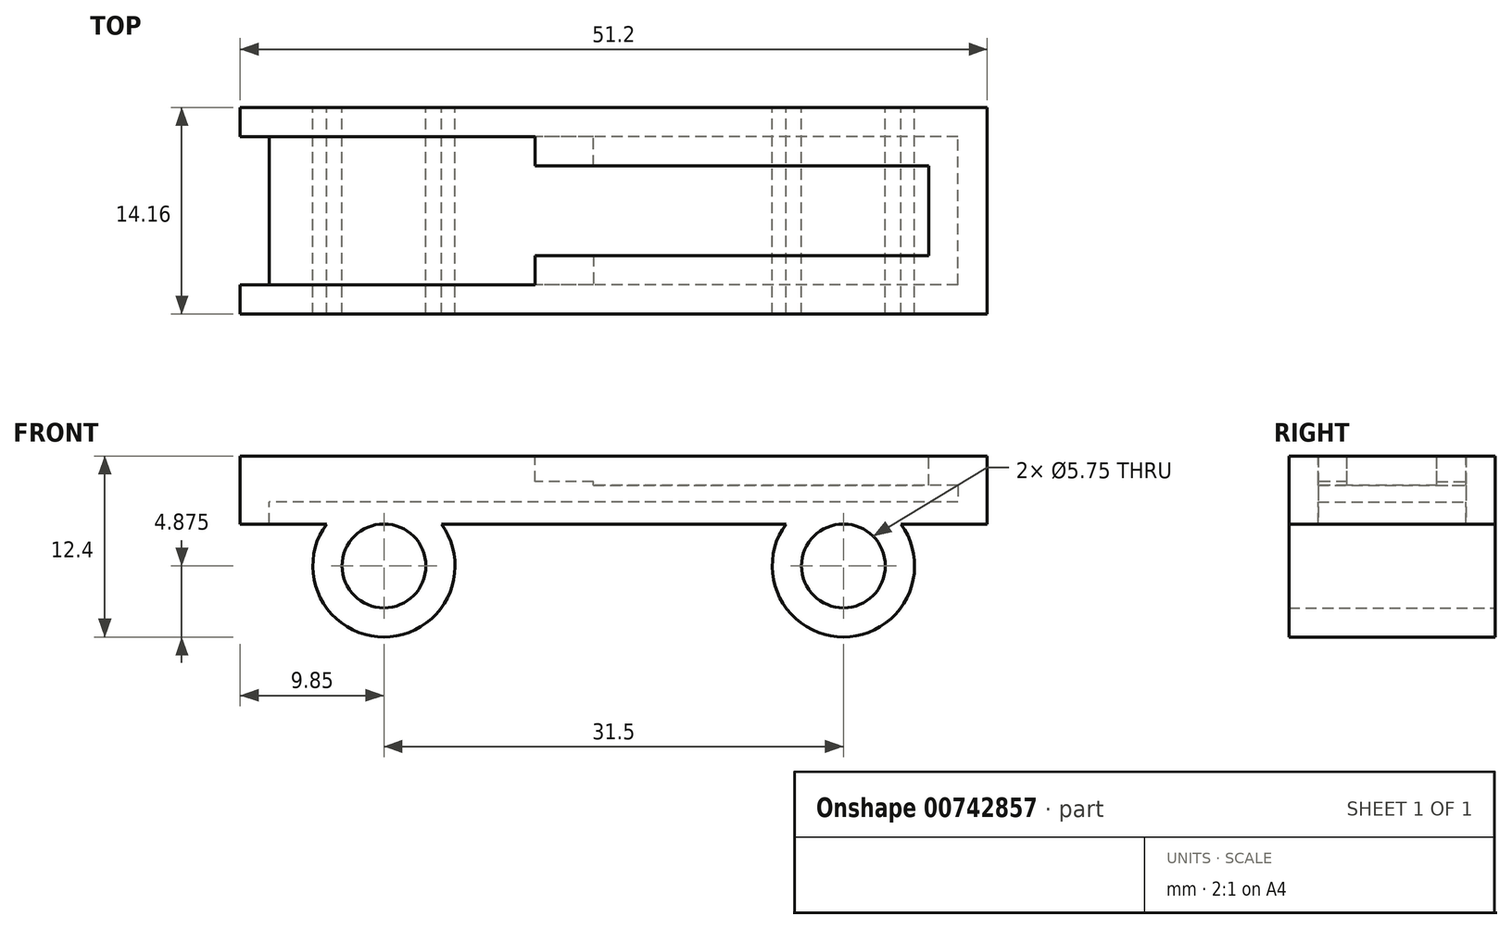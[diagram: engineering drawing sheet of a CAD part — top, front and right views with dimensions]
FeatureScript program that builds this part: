
annotation { "Feature Type Name" : "Feature", "Feature Type Description" : "" }
export const myFeature = defineFeature(function(context is Context, id is Id, definition is map)
    precondition{}
    {
        {
            var Q0;
            Q0=qCreatedBy(makeId("Top.planeOp"),FACE);
            var sketch = newSketch(context, id + "F0", { "sketchPlane" : qUnion([Q0])});
            skLineSegment(sketch, "E0.bottom", {"start": v(23.6, -5.07) * mm, "end": v(-23.6, -5.08) * mm});
            skLineSegment(sketch, "E0.top", {"start": v(23.6, 5.08) * mm, "end": v(-23.6, 5.07) * mm});
            skLineSegment(sketch, "E0.left", {"start": v(23.6, -5.07) * mm, "end": v(23.6, 5.08) * mm});
            skLineSegment(sketch, "E0.right", {"start": v(-23.6, -5.08) * mm, "end": v(-23.6, 5.07) * mm});
            skPoint(sketch, "E0.middle", {"position": v(0, 0) * mm});
            skLineSegment(sketch, "E1.0", {"start": v(-25.6, -7.08) * mm, "end": v(-25.6, 7.07) * mm});
            skLineSegment(sketch, "E1.1", {"start": v(25.6, -7.08) * mm, "end": v(-25.6, -7.08) * mm});
            skLineSegment(sketch, "E1.2", {"start": v(25.6, -7.07) * mm, "end": v(25.6, 7.08) * mm});
            skLineSegment(sketch, "E1.3", {"start": v(25.6, 7.08) * mm, "end": v(-25.6, 7.07) * mm});
            skLineSegment(sketch, "E2", {"start": v(-23.6, 5.07) * mm, "end": v(-25.6, 5.07) * mm});
            skLineSegment(sketch, "E3", {"start": v(-23.6, -5.08) * mm, "end": v(-25.6, -5.08) * mm});
            skSolve(sketch);
        }
        {
            var Q0;
            Q0=makeQuery(id+"F0.imprint","IMPRINT",FACE,{"disambiguationData":[TD([[makeQuery(id+"F0.imprint","IMPRINT",EDGE,{"derivedFrom":sQuery(id+"F0.wireOp",EDGE,"E0.bottom")}),1.0]])]});
            extrude(context, id + "F1", {"entities" : qUnion([Q0]), "depth" : 3.15 * mm, "offsetDistance" : 25 * mm});
        }
        {
            var Q0;
            Q0=makeQuery(id+"F1.opExtrude","CAP_FACE",FACE,{"disambiguationData":[OSD([sQuery(id+"F0.wireOp",EDGE,"E0.bottom"),sQuery(id+"F0.wireOp",EDGE,"E0.top"),sQuery(id+"F0.wireOp",EDGE,"E0.left"),sQuery(id+"F0.wireOp",EDGE,"E1.0"),sQuery(id+"F0.wireOp",EDGE,"E1.1"),sQuery(id+"F0.wireOp",EDGE,"E1.2"),sQuery(id+"F0.wireOp",EDGE,"E1.3"),sQuery(id+"F0.wireOp",EDGE,"E2"),sQuery(id+"F0.wireOp",EDGE,"E3")])],"isStart":false});
            var sketch = newSketch(context, id + "F2", { "sketchPlane" : qUnion([Q0])});
            skLineSegment(sketch, "E4", {"start": v(-25.6, 5.07) * mm, "end": v(-25.6, 3.07) * mm});
            skLineSegment(sketch, "E5", {"start": v(-25.6, 3.07) * mm, "end": v(21.6, 3.07) * mm});
            skLineSegment(sketch, "E6", {"start": v(21.6, 3.07) * mm, "end": v(21.6, -3.07) * mm});
            skLineSegment(sketch, "E7", {"start": v(21.6, -3.07) * mm, "end": v(-25.6, -3.07) * mm});
            skLineSegment(sketch, "E8", {"start": v(-25.6, -3.07) * mm, "end": v(-25.6, -5.08) * mm});
            skLineSegment(sketch, "E9", {"start": v(23.6, -3.07) * mm, "end": v(-1.4, -3.07) * mm});
            skLineSegment(sketch, "E10", {"start": v(-1.4, -3.07) * mm, "end": v(-1.4, -5.08) * mm});
            skLineSegment(sketch, "E11", {"start": v(-1.4, -3.07) * mm, "end": v(-5.4, -3.07) * mm});
            skLineSegment(sketch, "E12", {"start": v(-5.4, -3.07) * mm, "end": v(-5.4, -5.07) * mm});
            skLineSegment(sketch, "E13", {"start": v(-1.4, 3.07) * mm, "end": v(-1.4, 5.07) * mm});
            skLineSegment(sketch, "E14", {"start": v(-5.4, 3.07) * mm, "end": v(-5.4, 5.07) * mm});
            skSolve(sketch);
        }
        {
            var Q0;
            Q0=makeQuery(id+"F0.imprint","IMPRINT",FACE,{"disambiguationData":[TD([[makeQuery(id+"F0.imprint","IMPRINT",EDGE,{"derivedFrom":sQuery(id+"F0.wireOp",EDGE,"E0.bottom")}),-1.0]])]});
            var Q1;
            Q1=makeQuery(id+"F0.imprint","IMPRINT",FACE,{"disambiguationData":[TD([[makeQuery(id+"F0.imprint","IMPRINT",EDGE,{"derivedFrom":sQuery(id+"F0.wireOp",EDGE,"E0.bottom")}),1.0]])]});
            extrude(context, id + "F3", {"entities" : qUnion([Q0, Q1]), "operationType" : NewBodyOperationType.ADD, "oppositeDirection" : true, "depth" : 1.5 * mm, "offsetDistance" : 25 * mm});
        }
        {
            var Q0;
            {var subQ3=sQuery(id+"F2.wireOp",EDGE,"E10");Q0=makeQuery(id+"F2.imprint","IMPRINT",FACE,{"disambiguationData":[TD([[makeQuery(id+"F2.imprint","IMPRINT",EDGE,{"derivedFrom":subQ3}),1.0]])]});}
            var Q1;
            {var subQ2=sQuery(id+"F2.wireOp",EDGE,"E6");Q1=makeQuery(id+"F2.imprint","IMPRINT",FACE,{"disambiguationData":[TD([[makeQuery(id+"F2.imprint","IMPRINT",EDGE,{"derivedFrom":subQ2}),1.0]])]});}
            extrude(context, id + "F4", {"entities" : qUnion([Q0, Q1]), "operationType" : NewBodyOperationType.ADD, "oppositeDirection" : true, "depth" : 2 * mm, "offsetDistance" : 25 * mm});
        }
        {
            var Q0;
            {var subQ0=sQuery(id+"F2.wireOp",EDGE,"E10");Q0=makeQuery(id+"F2.imprint","IMPRINT",FACE,{"disambiguationData":[TD([[makeQuery(id+"F2.imprint","IMPRINT",EDGE,{"derivedFrom":subQ0}),-1.0]])]});}
            var Q1;
            {var subQ0=sQuery(id+"F2.wireOp",EDGE,"E13");Q1=makeQuery(id+"F2.imprint","IMPRINT",FACE,{"disambiguationData":[TD([[makeQuery(id+"F2.imprint","IMPRINT",EDGE,{"derivedFrom":subQ0}),1.0]])]});}
            extrude(context, id + "F5", {"entities" : qUnion([Q0, Q1]), "operationType" : NewBodyOperationType.ADD, "oppositeDirection" : true, "depth" : 1.75 * mm, "offsetDistance" : 25 * mm});
        }
        {
            var Q0;
            {var subQ0=sQuery(id+"F0.wireOp",EDGE,"E1.3");Q0=makeQuery(id+"F3.boolean.opBoolean","MERGE",FACE,{"derivedFrom":[makeQuery(id+"F1.opExtrude","SWEPT_FACE",FACE,{"disambiguationData":[OSD([subQ0])]}),makeQuery(id+"F3.opExtrude","SWEPT_FACE",FACE,{"disambiguationData":[OSD([subQ0])]})]});}
            var sketch = newSketch(context, id + "F6", { "sketchPlane" : qUnion([Q0])});
            skLineSegment(sketch, "E15", {"start": v(-18.25, -1.5) * mm, "end": v(18.25, -1.5) * mm});
            skLineSegment(sketch, "E16", {"start": v(-18.25, -1.5) * mm, "end": v(-15.75, -1.5) * mm});
            skLineSegment(sketch, "E17", {"start": v(18.25, -1.5) * mm, "end": v(15.75, -1.5) * mm});
            skLineSegment(sketch, "E18", {"start": v(15.75, -1.5) * mm, "end": v(15.75, -4.38) * mm});
            skLineSegment(sketch, "E19", {"start": v(-15.75, -1.5) * mm, "end": v(-15.75, -4.38) * mm});
            skLineSegment(sketch, "E20", {"start": v(-12, -1.5) * mm, "end": v(-19.5, -1.5) * mm});
            skLineSegment(sketch, "E21", {"start": v(12, -1.5) * mm, "end": v(19.5, -1.5) * mm});
            skLineSegment(sketch, "E22", {"start": v(17.81, 0) * mm, "end": v(13.69, 0) * mm});
            skLineSegment(sketch, "E23", {"start": v(-13.69, 0) * mm, "end": v(-17.81, 0) * mm});
            skCircle(sketch, "E24", {"center": v(15.75, -4.38) * mm, "radius": 2.88 * mm});
            skCircle(sketch, "E25", {"center": v(-15.75, -4.38) * mm, "radius": 2.88 * mm});
            skCircle(sketch, "E26.0", {"center": v(15.75, -4.38) * mm, "radius": 4.87 * mm});
            skCircle(sketch, "E27.0", {"center": v(-15.75, -4.38) * mm, "radius": 4.88 * mm});
            skLineSegment(sketch, "E28", {"start": v(17.9, 0) * mm, "end": v(17.81, 0) * mm});
            skLineSegment(sketch, "E29", {"start": v(13.69, 0) * mm, "end": v(13.6, 0) * mm});
            skLineSegment(sketch, "E30", {"start": v(-13.6, 0) * mm, "end": v(-13.69, 0) * mm});
            skLineSegment(sketch, "E31", {"start": v(-17.81, 0) * mm, "end": v(-17.9, 0) * mm});
            skSolve(sketch);
        }
        {
            var Q0;
            {var subQ6=sQuery(id+"F6.wireOp",EDGE,"E24");Q0=makeQuery(id+"F6.imprint","IMPRINT",FACE,{"disambiguationData":[TD([[makeQuery(id+"F6.imprint","IMPRINT",EDGE,{"derivedFrom":subQ6}),-1.0]])]});}
            var Q1;
            Q1=makeQuery(id+"F6.imprint","IMPRINT",FACE,{"disambiguationData":[TD([[makeQuery(id+"F6.imprint","IMPRINT",EDGE,{"derivedFrom":sQuery(id+"F6.wireOp",EDGE,"E22")}),1.0]])]});
            var Q2;
            Q2=makeQuery(id+"F6.imprint","IMPRINT",FACE,{"disambiguationData":[TD([[makeQuery(id+"F6.imprint","IMPRINT",EDGE,{"derivedFrom":sQuery(id+"F6.wireOp",EDGE,"E23")}),1.0]])]});
            var Q3;
            {var subQ0=sQuery(id+"F6.wireOp",EDGE,"E25");Q3=makeQuery(id+"F6.imprint","IMPRINT",FACE,{"disambiguationData":[TD([[makeQuery(id+"F6.imprint","IMPRINT",EDGE,{"derivedFrom":subQ0}),-1.0]])]});}
            extrude(context, id + "F7", {"entities" : qUnion([Q0, Q1, Q2, Q3]), "operationType" : NewBodyOperationType.ADD, "oppositeDirection" : true, "depth" : 14.15 * mm, "offsetDistance" : 25 * mm});
        }
    });
